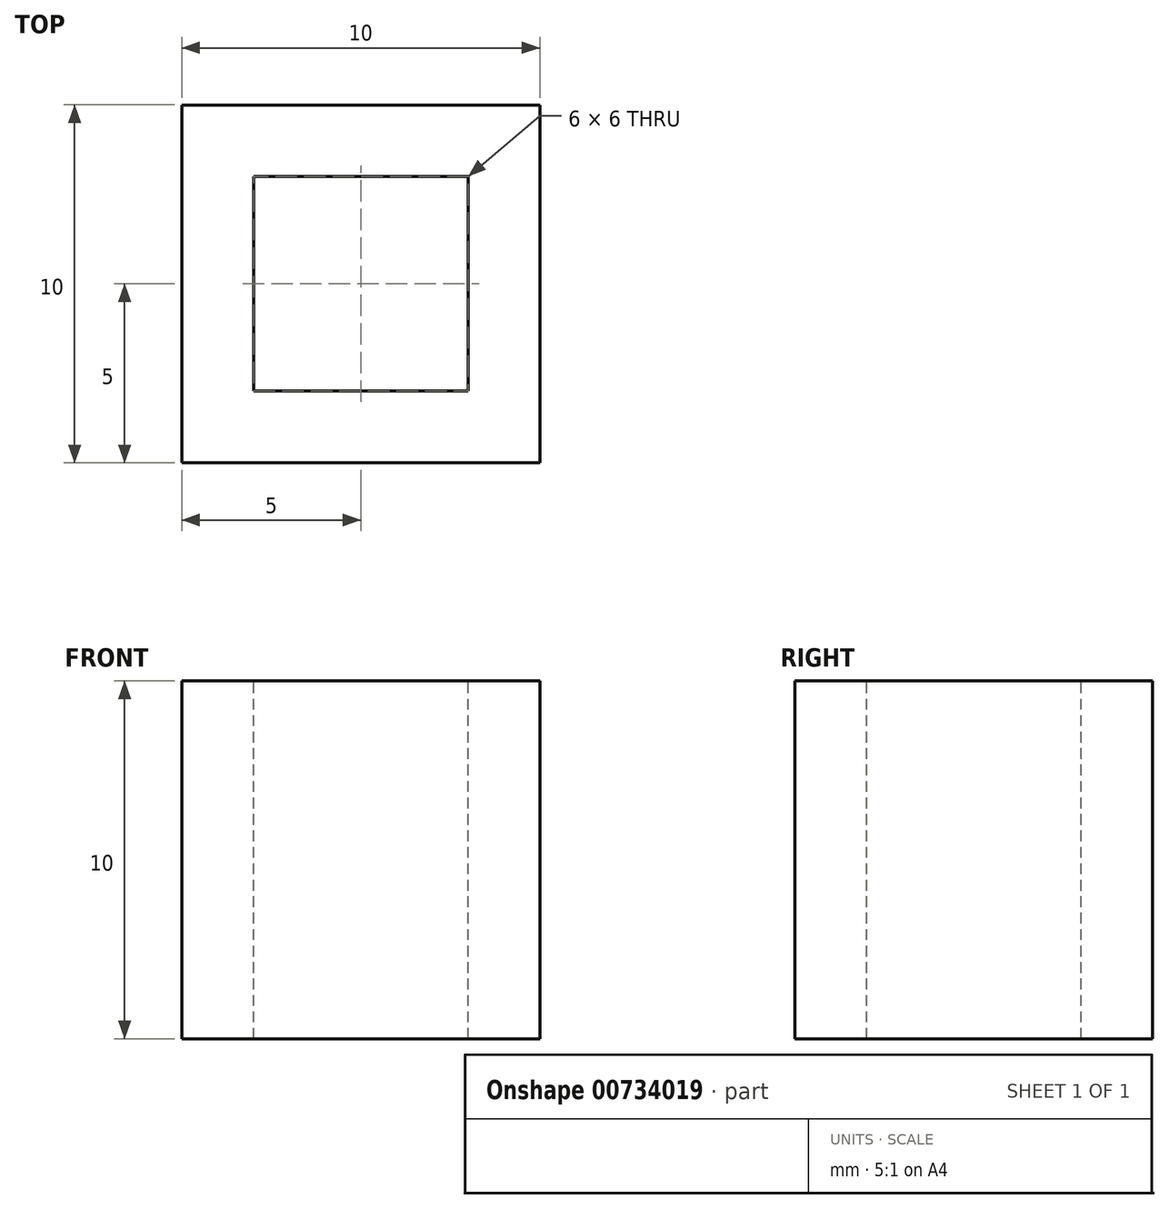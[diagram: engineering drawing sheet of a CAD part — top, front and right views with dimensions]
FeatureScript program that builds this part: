
annotation { "Feature Type Name" : "Feature", "Feature Type Description" : "" }
export const myFeature = defineFeature(function(context is Context, id is Id, definition is map)
    precondition{}
    {
        {
            var Q0;
            Q0=qCreatedBy(makeId("Top.planeOp"),FACE);
            var sketch = newSketch(context, id + "F0", { "sketchPlane" : qUnion([Q0])});
            skLineSegment(sketch, "E0.bottom", {"start": v(-3.53, 5.67) * mm, "end": v(6.47, 5.67) * mm});
            skLineSegment(sketch, "E0.top", {"start": v(-3.53, -4.33) * mm, "end": v(6.47, -4.33) * mm});
            skLineSegment(sketch, "E0.left", {"start": v(-3.53, 5.67) * mm, "end": v(-3.53, -4.33) * mm});
            skLineSegment(sketch, "E0.right", {"start": v(6.47, 5.67) * mm, "end": v(6.47, -4.33) * mm});
            skSolve(sketch);
        }
        {
            var Q0;
            Q0 = qSketchRegion(id + "F0", true);
            extrude(context, id + "F1", {"entities" : qUnion([Q0]), "depth" : 10 * mm, "offsetDistance" : 25 * mm});
        }
        {
            var Q0;
            Q0=makeQuery(id+"F1.opExtrude","CAP_FACE",FACE,{"disambiguationData":[OSD([sQuery(id+"F0.wireOp",EDGE,"E0.bottom"),sQuery(id+"F0.wireOp",EDGE,"E0.top"),sQuery(id+"F0.wireOp",EDGE,"E0.left"),sQuery(id+"F0.wireOp",EDGE,"E0.right")])],"isStart":false});
            var sketch = newSketch(context, id + "F2", { "sketchPlane" : qUnion([Q0])});
            skLineSegment(sketch, "E1.bottom", {"start": v(-1.53, 3.67) * mm, "end": v(4.47, 3.67) * mm});
            skLineSegment(sketch, "E1.top", {"start": v(-1.53, -2.33) * mm, "end": v(4.47, -2.33) * mm});
            skLineSegment(sketch, "E1.left", {"start": v(-1.53, 3.67) * mm, "end": v(-1.53, -2.33) * mm});
            skLineSegment(sketch, "E1.right", {"start": v(4.47, 3.67) * mm, "end": v(4.47, -2.33) * mm});
            skPoint(sketch, "E2", {"position": v(1.47, 3.67) * mm});
            skPoint(sketch, "E3", {"position": v(-1.53, 0.67) * mm});
            skSolve(sketch);
        }
        {
            var Q0;
            Q0 = qSketchRegion(id + "F2", true);
            extrude(context, id + "F3", {"entities" : qUnion([Q0]), "operationType" : NewBodyOperationType.REMOVE, "oppositeDirection" : true, "depth" : 25 * mm, "offsetDistance" : 25 * mm});
        }
    });
